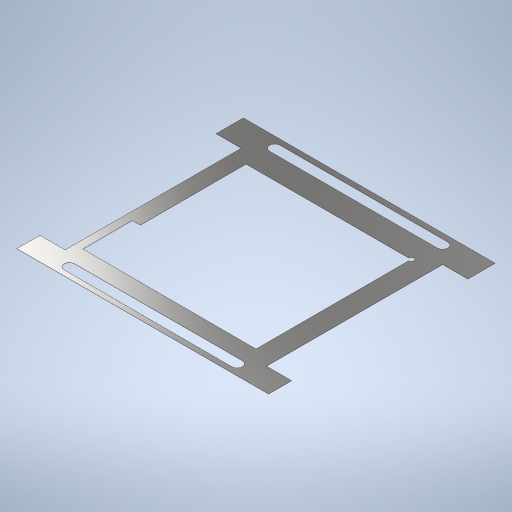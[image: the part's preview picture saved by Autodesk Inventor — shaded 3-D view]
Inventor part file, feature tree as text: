
AUTODESK INVENTOR PART (.ipt)
format: ipt  version: 2023 (Build 270158000, 158)  size: 327,168 bytes
history: native  units: in
note: dims shown in document units (in); Inventor stores cm internally (conversion verified against a paired STEP export)
features: extrude x5, sketch x5
ambient origin geometry x8: Origin, YZ Plane, XZ Plane, XY Plane, X Axis, Y Axis, Z Axis, Center Point
bodies: Solid1 (feature_tree)
feature tree (10):
  extrude  "Extrusion1"  Depth=2.7in
  extrude  "Extrusion2"  TaperAngle=0.0deg  [1 undecoded]
  extrude  "Extrusion3"  Depth=0.3in
  extrude  "Extrusion4"  Depth=0.125in
  extrude  "Extrusion5"  Depth=1.9685in
  sketch  "Sketch1"  dims[d0=3.0in d1=2.7in]
  sketch  "Sketch2"  dims[d2=0.002in d3=0.0in d7=0.0in d8=0.0in]
  sketch  "Sketch3"  dims[d13=2.1in d14=0.3in]
  sketch  "Sketch4"  dims[d16=0.325in d17=0.125in]
  sketch  "Sketch5"  dims[d18=0.125in d19=2.0in d20=2.0in d21=0.125in d22=0.125in d23=1.0in d24=0.0in d27=0.0in d28=0.0in d29=0.0625in d30=0.5906in d31=0.1919in d32=0.096in d33=0.0in d34=0.0in d35=2.35in d36=1.8in d37=0.2146in d38=0.0098in d39=1.8504in d40=1.9685in]
note: 1 required parameter value undecoded (feature->parameter linkage not recoverable at this tier; creation-order binding heuristic only, values carry confidence <= 0.55)
